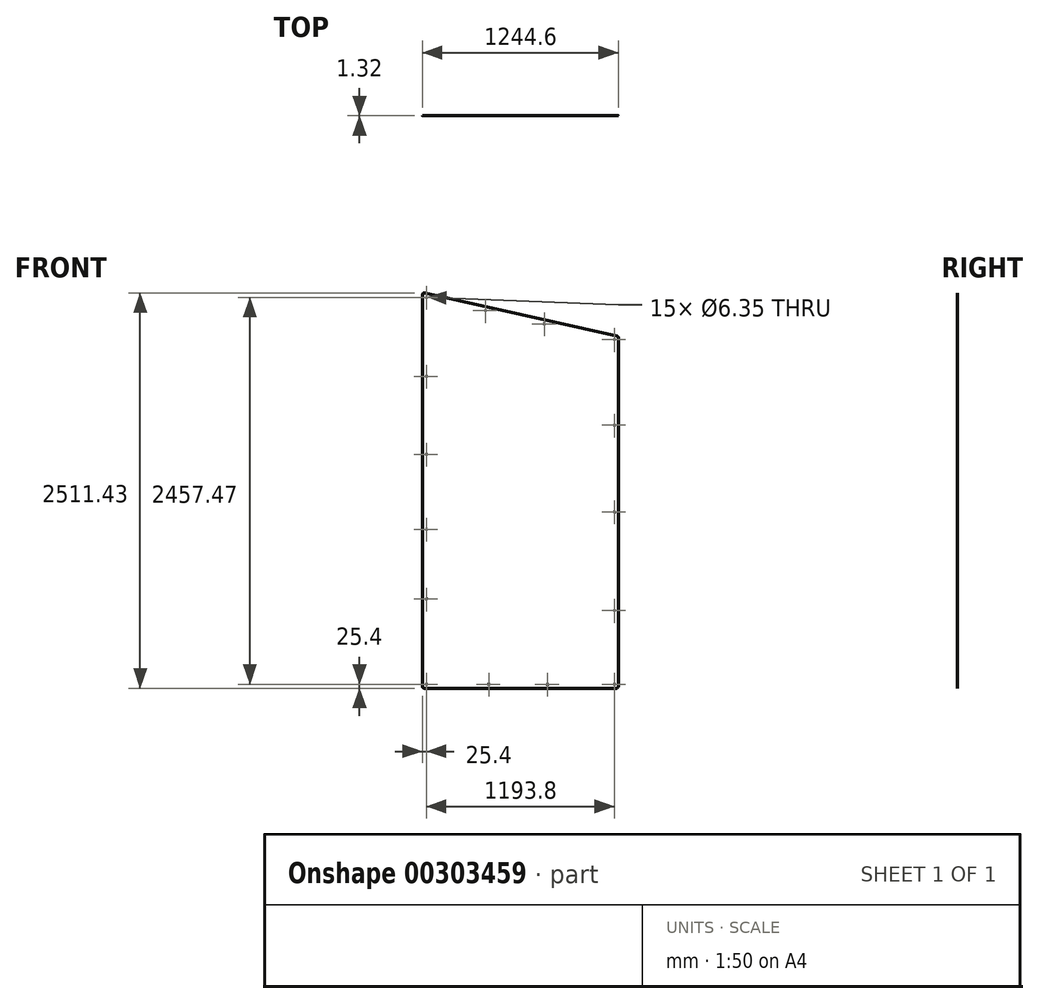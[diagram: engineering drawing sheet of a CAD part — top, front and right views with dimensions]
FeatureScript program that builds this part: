
annotation { "Feature Type Name" : "Feature", "Feature Type Description" : "" }
export const myFeature = defineFeature(function(context is Context, id is Id, definition is map)
    precondition{}
    {
        {
            var Q0;
            Q0=qCreatedBy(makeId("Front.planeOp"),FACE);
            var sketch = newSketch(context, id + "F0", { "sketchPlane" : qUnion([Q0])});
            skLineSegment(sketch, "E0", {"start": v(0, 0) * mm, "end": v(1244.6, 0) * mm});
            skLineSegment(sketch, "E1", {"start": v(1244.6, 0) * mm, "end": v(1244.6, 2235.2) * mm});
            skLineSegment(sketch, "E2", {"start": v(1244.6, 2235.2) * mm, "end": v(0, 2514.6) * mm});
            skLineSegment(sketch, "E3", {"start": v(0, 2514.6) * mm, "end": v(0, 0) * mm});
            skSolve(sketch);
        }
        {
            var Q0;
            Q0 = qSketchRegion(id + "F0", true);
            extrude(context, id + "F1", {"entities" : qUnion([Q0]), "depth" : 1.32 * mm});
        }
        {
            var Q0;
            Q0=makeQuery(id+"F1.opExtrude","CAP_FACE",FACE,{"disambiguationData":[OSD([sQuery(id+"F0.wireOp",EDGE,"E0"),sQuery(id+"F0.wireOp",EDGE,"E1"),sQuery(id+"F0.wireOp",EDGE,"E2"),sQuery(id+"F0.wireOp",EDGE,"E3")])],"isStart":false});
            var sketch = newSketch(context, id + "F2", { "sketchPlane" : qUnion([Q0])});
            skLineSegment(sketch, "E4.0", {"start": v(1219.2, 2214.87) * mm, "end": v(25.4, 2482.87) * mm, "construction": true});
            skLineSegment(sketch, "E4.1", {"start": v(1219.2, 25.4) * mm, "end": v(1219.2, 2214.87) * mm, "construction": true});
            skLineSegment(sketch, "E4.2", {"start": v(25.4, 25.4) * mm, "end": v(1219.2, 25.4) * mm, "construction": true});
            skLineSegment(sketch, "E4.3", {"start": v(25.4, 2482.87) * mm, "end": v(25.4, 25.4) * mm, "construction": true});
            skCircle(sketch, "E5", {"center": v(25.4, 2482.87) * mm, "radius": 3.18 * mm});
            skCircle(sketch, "E6", {"center": v(1219.2, 2214.87) * mm, "radius": 3.18 * mm});
            skCircle(sketch, "E7", {"center": v(399.95, 2398.78) * mm, "radius": 3.18 * mm});
            skCircle(sketch, "E8", {"center": v(774.5, 2314.7) * mm, "radius": 3.18 * mm});
            skCircle(sketch, "E9", {"center": v(1219.2, 25.4) * mm, "radius": 3.18 * mm});
            skCircle(sketch, "E10", {"center": v(25.4, 25.4) * mm, "radius": 3.18 * mm});
            skCircle(sketch, "E11", {"center": v(421.26, 25.4) * mm, "radius": 3.18 * mm});
            skCircle(sketch, "E12", {"center": v(794.35, 25.4) * mm, "radius": 3.18 * mm});
            skCircle(sketch, "E13", {"center": v(1219.2, 1120.13) * mm, "radius": 3.18 * mm});
            skCircle(sketch, "E14", {"center": v(1219.2, 1671.08) * mm, "radius": 3.18 * mm});
            skCircle(sketch, "E15", {"center": v(1219.2, 494.01) * mm, "radius": 3.18 * mm});
            skCircle(sketch, "E16", {"center": v(25.4, 1485.75) * mm, "radius": 3.18 * mm});
            skCircle(sketch, "E17", {"center": v(25.4, 1009.67) * mm, "radius": 3.18 * mm});
            skCircle(sketch, "E18", {"center": v(25.4, 566.67) * mm, "radius": 3.18 * mm});
            skCircle(sketch, "E19", {"center": v(25.4, 1981.02) * mm, "radius": 3.18 * mm});
            skSolve(sketch);
        }
        {
            var Q0;
            Q0 = qSketchRegion(id + "F2", true);
            extrude(context, id + "F3", {"entities" : qUnion([Q0]), "operationType" : NewBodyOperationType.REMOVE, "oppositeDirection" : true, "depth" : 25.4 * mm});
        }
        {
            var Q0;
            Q0=makeQuery(id+"F1.opExtrude","SWEPT_EDGE",EDGE,{"disambiguationData":[OSD([sQuery(id+"F0.wireOp",EDGE,"E1"),sQuery(id+"F0.wireOp",EDGE,"E2")])]});
            var Q1;
            Q1=makeQuery(id+"F1.opExtrude","SWEPT_EDGE",EDGE,{"disambiguationData":[OSD([sQuery(id+"F0.wireOp",EDGE,"E2"),sQuery(id+"F0.wireOp",EDGE,"E3")])]});
            var Q2;
            Q2=makeQuery(id+"F1.opExtrude","SWEPT_EDGE",EDGE,{"disambiguationData":[OSD([sQuery(id+"F0.wireOp",EDGE,"E0"),sQuery(id+"F0.wireOp",EDGE,"E1")])]});
            var Q3;
            Q3=makeQuery(id+"F1.opExtrude","SWEPT_EDGE",EDGE,{"disambiguationData":[OSD([sQuery(id+"F0.wireOp",EDGE,"E0"),sQuery(id+"F0.wireOp",EDGE,"E3")])]});
            fillet(context, id + "F4", {"entities" : qUnion([Q0, Q1, Q2, Q3]), "radius" : 12.7 * mm, "tangentPropagation" : true, "allowEdgeOverflow" : false});
        }
    });
